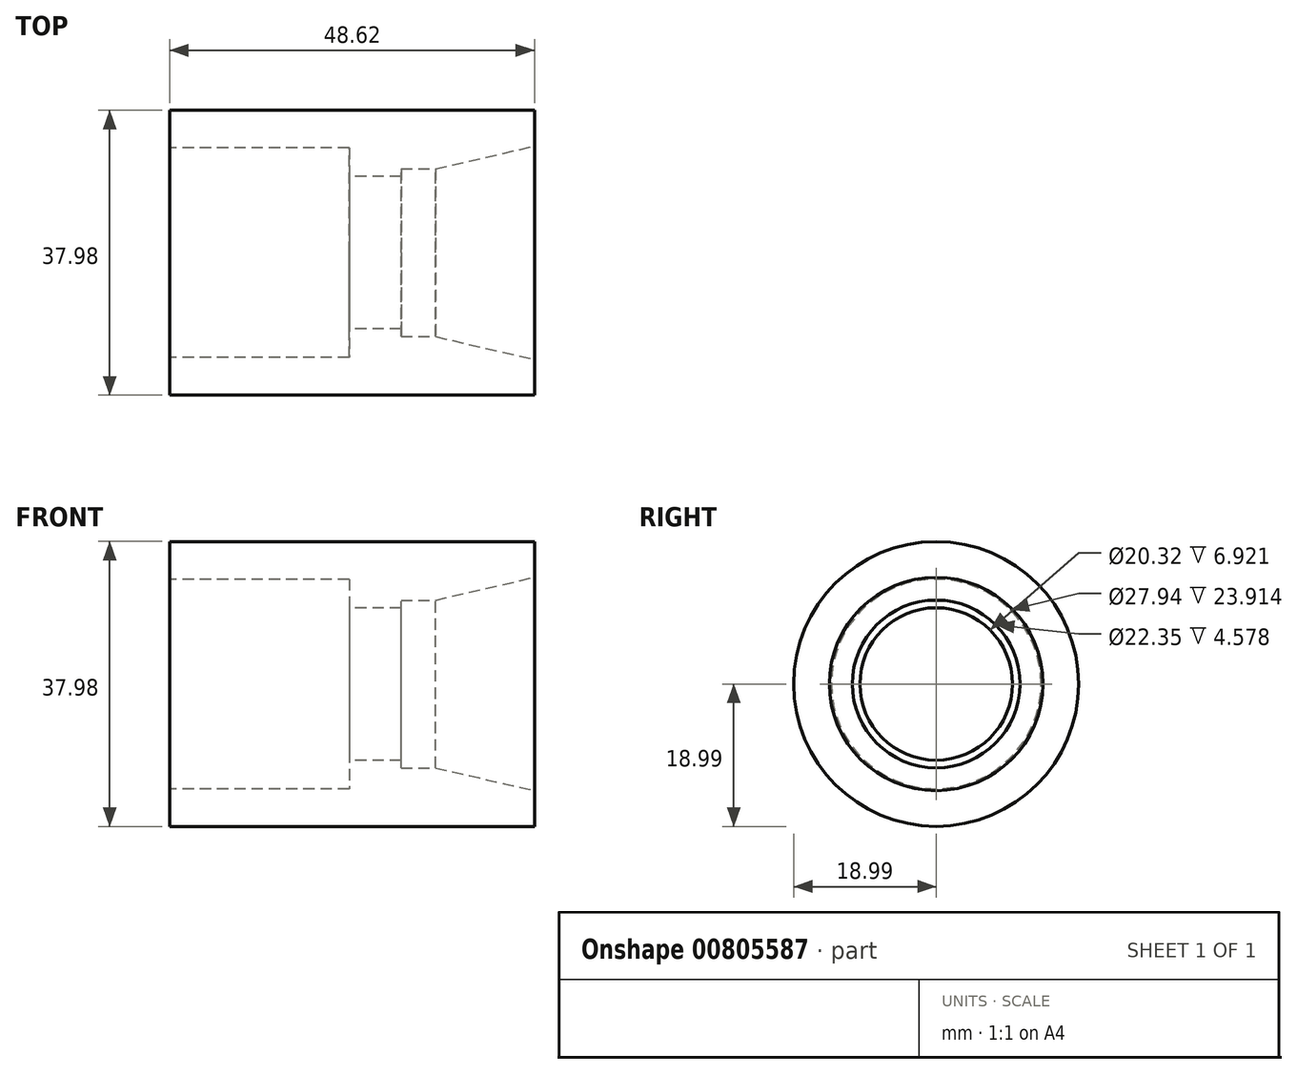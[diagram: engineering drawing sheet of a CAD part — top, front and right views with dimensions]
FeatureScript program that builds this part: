
annotation { "Feature Type Name" : "Feature", "Feature Type Description" : "" }
export const myFeature = defineFeature(function(context is Context, id is Id, definition is map)
    precondition{}
    {
        {
            var Q0;
            Q0=qCreatedBy(makeId("Right.planeOp"),FACE);
            var sketch = newSketch(context, id + "F0", { "sketchPlane" : qUnion([Q0])});
            skCircle(sketch, "E0", {"center": v(0, 0) * mm, "radius": 18.99 * mm});
            skSolve(sketch);
        }
        {
            var Q0;
            Q0 = qSketchRegion(id + "F0", true);
            extrude(context, id + "F1", {"entities" : qUnion([Q0]), "depth" : 48.62 * mm, "offsetDistance" : 25.4 * mm});
        }
        {
            var Q0;
            Q0=makeQuery(id+"F1.opExtrude","CAP_FACE",FACE,{"disambiguationData":[OSD([sQuery(id+"F0.wireOp",EDGE,"E0")])],"isStart":true});
            var sketch = newSketch(context, id + "F2", { "sketchPlane" : qUnion([Q0])});
            skCircle(sketch, "E1", {"center": v(0, 0) * mm, "radius": 13.97 * mm});
            skSolve(sketch);
        }
        {
            var Q0;
            Q0 = qSketchRegion(id + "F2", true);
            extrude(context, id + "F3", {"entities" : qUnion([Q0]), "operationType" : NewBodyOperationType.REMOVE, "oppositeDirection" : true, "depth" : 23.91 * mm, "offsetDistance" : 25.4 * mm});
        }
        {
            var Q0;
            Q0=makeQuery(id+"F3.boolean.opBoolean","COPY",FACE,{"derivedFrom":makeQuery(id+"F3.opExtrude","CAP_FACE",FACE,{"disambiguationData":[OSD([sQuery(id+"F2.wireOp",EDGE,"E1")])],"isStart":false})});
            var sketch = newSketch(context, id + "F4", { "sketchPlane" : qUnion([Q0])});
            skCircle(sketch, "E2", {"center": v(0, 0) * mm, "radius": 10.16 * mm});
            skSolve(sketch);
        }
        {
            var Q0;
            Q0 = qSketchRegion(id + "F4", true);
            extrude(context, id + "F5", {"entities" : qUnion([Q0]), "operationType" : NewBodyOperationType.REMOVE, "endBound" : BoundingType.THROUGH_ALL, "oppositeDirection" : true, "depth" : 25.4 * mm, "offsetDistance" : 25.4 * mm});
        }
        {
            var Q0;
            Q0=makeQuery(id+"F1.opExtrude","CAP_FACE",FACE,{"disambiguationData":[OSD([sQuery(id+"F0.wireOp",EDGE,"E0")])],"isStart":false});
            var sketch = newSketch(context, id + "F6", { "sketchPlane" : qUnion([Q0])});
            skCircle(sketch, "E3", {"center": v(0, 0) * mm, "radius": 11.18 * mm});
            skSolve(sketch);
        }
        {
            var Q0;
            Q0 = qSketchRegion(id + "F6", true);
            extrude(context, id + "F7", {"entities" : qUnion([Q0]), "operationType" : NewBodyOperationType.REMOVE, "oppositeDirection" : true, "depth" : 17.78 * mm, "offsetDistance" : 25.4 * mm});
        }
        {
            var Q0;
            Q0=makeQuery(id+"F1.opExtrude","CAP_FACE",FACE,{"disambiguationData":[OSD([sQuery(id+"F0.wireOp",EDGE,"E0")])],"isStart":false});
            var sketch = newSketch(context, id + "F8", { "sketchPlane" : qUnion([Q0])});
            skCircle(sketch, "E4", {"center": v(0, 0) * mm, "radius": 14.22 * mm});
            skSolve(sketch);
        }
        {
            var Q0;
            Q0 = qSketchRegion(id + "F8", true);
            extrude(context, id + "F9", {"entities" : qUnion([Q0]), "operationType" : NewBodyOperationType.REMOVE, "oppositeDirection" : true, "depth" : 17.78 * mm, "offsetDistance" : 25.4 * mm, "hasDraft" : true, "draftAngle" : 13 * degree, "draftPullDirection" : true});
        }
    });
